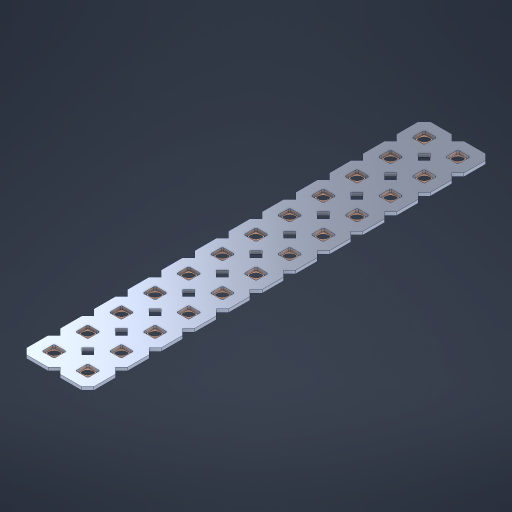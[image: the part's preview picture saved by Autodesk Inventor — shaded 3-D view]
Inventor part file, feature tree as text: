
AUTODESK INVENTOR PART (.ipt)
format: ipt  version: 2023 (Build 270158000, 158)  size: 528,384 bytes
history: native  units: in
note: dims shown in document units (in); Inventor stores cm internally (conversion verified against a paired STEP export)
features: other x25, extrude x23, sketch x2, pattern_linear x1
ambient origin geometry x8: Origin, YZ Plane, XZ Plane, XY Plane, X Axis, Y Axis, Z Axis, Center Point
bodies: Solid1 (feature_tree), Body (feature_tree)
feature tree (51):
  pattern_linear  "Rectangular Pattern1"  Spacing1=0.09in  [1 undecoded]
  sketch  "Sketch1"  dims[d1=0.5in]
  sketch  "Sketch2"  dims[d2=0.182in d3=0.09in d4=0.09in d5=0.09in d6=0.09in d7=0.09in d8=0.09in d9=0.09in d10=0.09in d11=0.02in d13=0.0in d14=0.172in d15=0.0625in d16=0.0in d19=0.5in d22=0.5in]
  other  "Srf1"
  other  "Srf126"
  other  "Srf127"
  other  "Srf128"
  other  "Srf129"
  other  "Srf130"
  other  "Srf131"
  other  "Srf250"
  other  "Srf251"
  other  "Srf252"
  other  "Srf253"
  other  "Srf254"
  other  "Srf268"
  other  "Srf269"
  other  "Srf270"
  other  "Srf271"
  other  "Srf272"
  other  "Srf273"
  other  "Srf274"
  other  "Srf275"
  other  "Srf276"
  other  "Srf277"
  other  "Srf278"
  other  "Srf279"
  other  "Circle"
  extrude  "ExtrusionSrf126"  Depth=0.09in
  extrude  "ExtrusionSrf127"  Depth=0.09in
  extrude  "ExtrusionSrf128"  Depth=0.09in
  extrude  "ExtrusionSrf129"  Depth=0.09in
  extrude  "ExtrusionSrf130"  Depth=0.09in
  extrude  "ExtrusionSrf131"  Depth=0.09in
  extrude  "ExtrusionSrf250"  Depth=0.09in
  extrude  "ExtrusionSrf251"  Depth=0.02in
  extrude  "ExtrusionSrf252"  TaperAngle=0.0deg  [1 undecoded]
  extrude  "ExtrusionSrf253"  Depth=0.5in
  extrude  "ExtrusionSrf254"  Depth=0.5in TaperAngle=0.0deg
  extrude  "ExtrusionSrf268"  Depth=0.5in
  extrude  "ExtrusionSrf269"  Depth=0.5in
  extrude  "ExtrusionSrf270"  [1 undecoded]
  extrude  "ExtrusionSrf271"  [1 undecoded]
  extrude  "ExtrusionSrf272"  [1 undecoded]
  extrude  "ExtrusionSrf273"  [1 undecoded]
  extrude  "ExtrusionSrf274"  [1 undecoded]
  extrude  "ExtrusionSrf275"  [1 undecoded]
  extrude  "ExtrusionSrf276"  [1 undecoded]
  extrude  "ExtrusionSrf277"  [1 undecoded]
  extrude  "ExtrusionSrf278"  [1 undecoded]
  extrude  "ExtrusionSrf279"  [1 undecoded]
note: 12 required parameter values undecoded (feature->parameter linkage not recoverable at this tier; creation-order binding heuristic only, values carry confidence <= 0.55)
